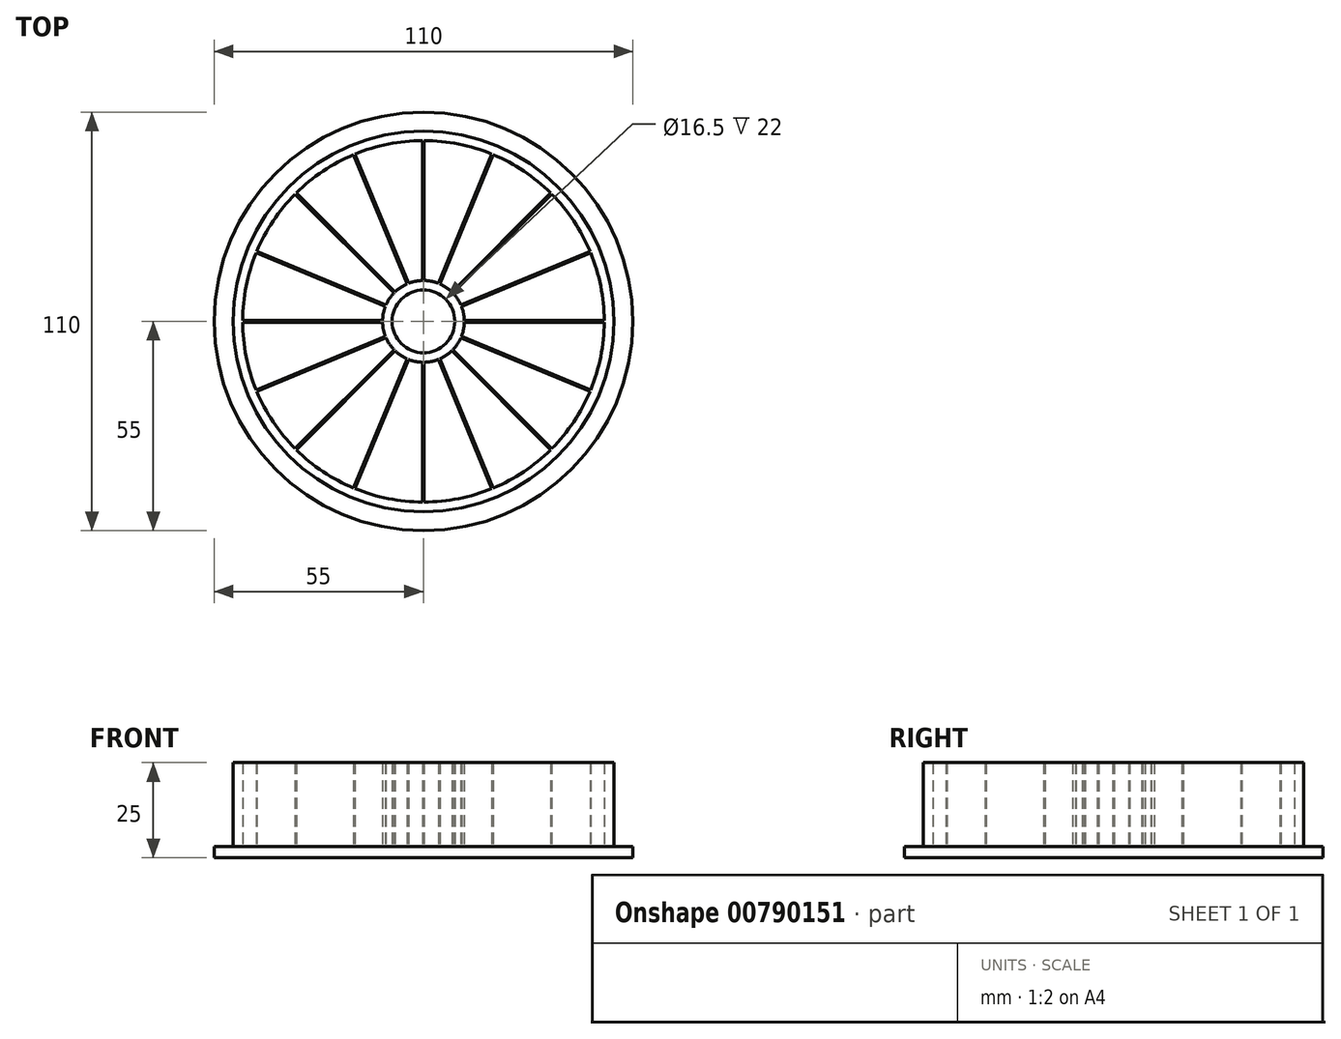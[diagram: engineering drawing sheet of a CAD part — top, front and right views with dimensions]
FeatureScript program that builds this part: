
annotation { "Feature Type Name" : "Feature", "Feature Type Description" : "" }
export const myFeature = defineFeature(function(context is Context, id is Id, definition is map)
    precondition{}
    {
        {
            var Q0;
            Q0=qCreatedBy(makeId("Top.planeOp"),FACE);
            var sketch = newSketch(context, id + "F0", { "sketchPlane" : qUnion([Q0])});
            skCircle(sketch, "E0", {"center": v(0, 0) * mm, "radius": 50 * mm});
            skArc(sketch, "E1", {"start": v(-0.2, 47.5) * mm, "mid": v(-9.27, 46.59) * mm, "end": v(-18, 43.96) * mm});
            skCircle(sketch, "E2", {"center": v(0, 0) * mm, "radius": 8.25 * mm});
            skArc(sketch, "E3", {"start": v(-0.2, 10.75) * mm, "mid": v(-2.1, 10.54) * mm, "end": v(-3.93, 10) * mm});
            skLineSegment(sketch, "E4", {"start": v(-0.2, 10.75) * mm, "end": v(-0.2, 47.5) * mm});
            skLineSegment(sketch, "E5", {"start": v(0.2, 10.75) * mm, "end": v(0.2, 47.5) * mm});
            skLineSegment(sketch, "E6.MirrorCS", {"start": v(-0.2, -10.75) * mm, "end": v(-0.2, -47.5) * mm});
            skLineSegment(sketch, "E7.MirrorCS", {"start": v(0.2, -10.75) * mm, "end": v(0.2, -47.5) * mm});
            skLineSegment(sketch, "E8", {"start": v(-5.83, -5.83) * mm, "end": v(5.83, 5.83) * mm, "construction": true});
            skLineSegment(sketch, "E9", {"start": v(-7.62, -3.16) * mm, "end": v(7.62, 3.16) * mm, "construction": true});
            skLineSegment(sketch, "E10", {"start": v(-8.1, -1.6) * mm, "end": v(8.1, 1.6) * mm, "construction": true});
            skLineSegment(sketch, "E11.MirrorCS", {"start": v(10.75, 0.2) * mm, "end": v(47.5, 0.2) * mm});
            skLineSegment(sketch, "E12.MirrorCS", {"start": v(10.75, -0.2) * mm, "end": v(47.5, -0.2) * mm});
            skLineSegment(sketch, "E13.MirrorCS", {"start": v(-10.75, 0.2) * mm, "end": v(-47.5, 0.2) * mm});
            skLineSegment(sketch, "E14.MirrorCS", {"start": v(-10.75, -0.2) * mm, "end": v(-47.5, -0.2) * mm});
            skLineSegment(sketch, "E15.MirrorCS", {"start": v(7.46, -7.74) * mm, "end": v(33.45, -33.73) * mm});
            skLineSegment(sketch, "E16.MirrorCS", {"start": v(7.74, -7.46) * mm, "end": v(33.73, -33.45) * mm});
            skLineSegment(sketch, "E17.MirrorCS", {"start": v(7.74, 7.46) * mm, "end": v(33.73, 33.45) * mm});
            skLineSegment(sketch, "E18.MirrorCS", {"start": v(7.46, 7.74) * mm, "end": v(33.45, 33.73) * mm});
            skLineSegment(sketch, "E19.MirrorCS", {"start": v(-7.46, 7.74) * mm, "end": v(-33.45, 33.73) * mm});
            skLineSegment(sketch, "E20.MirrorCS", {"start": v(-7.74, 7.46) * mm, "end": v(-33.73, 33.45) * mm});
            skLineSegment(sketch, "E21.MirrorCS", {"start": v(-7.74, -7.46) * mm, "end": v(-33.73, -33.45) * mm});
            skLineSegment(sketch, "E22.MirrorCS", {"start": v(-7.46, -7.74) * mm, "end": v(-33.45, -33.73) * mm});
            skLineSegment(sketch, "E23.MirrorCS", {"start": v(3.93, -10) * mm, "end": v(18, -43.96) * mm});
            skLineSegment(sketch, "E24.MirrorCS", {"start": v(4.3, -9.85) * mm, "end": v(18.36, -43.8) * mm});
            skLineSegment(sketch, "E25.MirrorCS", {"start": v(9.85, -4.3) * mm, "end": v(43.8, -18.36) * mm});
            skLineSegment(sketch, "E26.MirrorCS", {"start": v(10, -3.93) * mm, "end": v(43.96, -18) * mm});
            skLineSegment(sketch, "E27.MirrorCS", {"start": v(10, 3.93) * mm, "end": v(43.96, 18) * mm});
            skLineSegment(sketch, "E28.MirrorCS", {"start": v(9.85, 4.3) * mm, "end": v(43.8, 18.36) * mm});
            skLineSegment(sketch, "E29.MirrorCS", {"start": v(4.3, 9.85) * mm, "end": v(18.36, 43.8) * mm});
            skLineSegment(sketch, "E30.MirrorCS", {"start": v(3.93, 10) * mm, "end": v(18, 43.96) * mm});
            skLineSegment(sketch, "E31.MirrorCS", {"start": v(-3.93, 10) * mm, "end": v(-18, 43.96) * mm});
            skLineSegment(sketch, "E32.MirrorCS", {"start": v(-4.3, 9.85) * mm, "end": v(-18.36, 43.8) * mm});
            skLineSegment(sketch, "E33.MirrorCS", {"start": v(-9.85, 4.3) * mm, "end": v(-43.8, 18.36) * mm});
            skLineSegment(sketch, "E34.MirrorCS", {"start": v(-10, 3.93) * mm, "end": v(-43.96, 18) * mm});
            skLineSegment(sketch, "E35.MirrorCS", {"start": v(-10, -3.93) * mm, "end": v(-43.96, -18) * mm});
            skLineSegment(sketch, "E36.MirrorCS", {"start": v(-9.85, -4.3) * mm, "end": v(-43.8, -18.36) * mm});
            skLineSegment(sketch, "E37.MirrorCS", {"start": v(-4.3, -9.85) * mm, "end": v(-18.36, -43.8) * mm});
            skLineSegment(sketch, "E38.MirrorCS", {"start": v(-3.93, -10) * mm, "end": v(-18, -43.96) * mm});
            skArc(sketch, "E39.trimOffspring", {"start": v(18, 43.96) * mm, "mid": v(9.27, 46.59) * mm, "end": v(0.2, 47.5) * mm});
            skArc(sketch, "E40.trimOffspring", {"start": v(33.45, 33.73) * mm, "mid": v(26.39, 39.5) * mm, "end": v(18.36, 43.8) * mm});
            skArc(sketch, "E41.trimOffspring", {"start": v(47.5, 0.2) * mm, "mid": v(46.59, 9.27) * mm, "end": v(43.96, 18) * mm});
            skArc(sketch, "E42.trimOffspring", {"start": v(43.8, 18.36) * mm, "mid": v(39.5, 26.39) * mm, "end": v(33.73, 33.45) * mm});
            skArc(sketch, "E43.trimOffspring", {"start": v(43.96, -18) * mm, "mid": v(46.59, -9.27) * mm, "end": v(47.5, -0.2) * mm});
            skArc(sketch, "E44.trimOffspring", {"start": v(33.73, -33.45) * mm, "mid": v(39.5, -26.39) * mm, "end": v(43.8, -18.36) * mm});
            skArc(sketch, "E45.trimOffspring", {"start": v(18.36, -43.8) * mm, "mid": v(26.39, -39.5) * mm, "end": v(33.45, -33.73) * mm});
            skArc(sketch, "E46.trimOffspring", {"start": v(0.2, -47.5) * mm, "mid": v(9.27, -46.59) * mm, "end": v(18, -43.96) * mm});
            skArc(sketch, "E47.trimOffspring", {"start": v(-18, -43.96) * mm, "mid": v(-9.27, -46.59) * mm, "end": v(-0.2, -47.5) * mm});
            skArc(sketch, "E48.trimOffspring", {"start": v(-33.45, -33.73) * mm, "mid": v(-26.39, -39.5) * mm, "end": v(-18.36, -43.8) * mm});
            skArc(sketch, "E49.trimOffspring", {"start": v(-43.8, -18.36) * mm, "mid": v(-39.5, -26.39) * mm, "end": v(-33.73, -33.45) * mm});
            skArc(sketch, "E50.trimOffspring", {"start": v(-47.5, -0.2) * mm, "mid": v(-46.59, -9.27) * mm, "end": v(-43.96, -18) * mm});
            skArc(sketch, "E51.trimOffspring", {"start": v(-43.96, 18) * mm, "mid": v(-46.59, 9.27) * mm, "end": v(-47.5, 0.2) * mm});
            skArc(sketch, "E52.trimOffspring", {"start": v(-18.36, 43.8) * mm, "mid": v(-26.39, 39.5) * mm, "end": v(-33.45, 33.73) * mm});
            skArc(sketch, "E53.trimOffspring", {"start": v(-33.73, 33.45) * mm, "mid": v(-39.5, 26.39) * mm, "end": v(-43.8, 18.36) * mm});
            skArc(sketch, "E54.trimOffspring", {"start": v(3.93, 10) * mm, "mid": v(2.1, 10.54) * mm, "end": v(0.2, 10.75) * mm});
            skArc(sketch, "E55.trimOffspring", {"start": v(7.46, 7.74) * mm, "mid": v(5.97, 8.94) * mm, "end": v(4.3, 9.85) * mm});
            skArc(sketch, "E56.trimOffspring", {"start": v(9.85, 4.3) * mm, "mid": v(8.94, 5.97) * mm, "end": v(7.74, 7.46) * mm});
            skArc(sketch, "E57.trimOffspring", {"start": v(10.75, 0.2) * mm, "mid": v(10.54, 2.1) * mm, "end": v(10, 3.93) * mm});
            skArc(sketch, "E58.trimOffspring", {"start": v(10, -3.93) * mm, "mid": v(10.54, -2.1) * mm, "end": v(10.75, -0.2) * mm});
            skArc(sketch, "E59.trimOffspring", {"start": v(7.74, -7.46) * mm, "mid": v(8.94, -5.97) * mm, "end": v(9.85, -4.3) * mm});
            skArc(sketch, "E60.trimOffspring", {"start": v(4.3, -9.85) * mm, "mid": v(5.97, -8.94) * mm, "end": v(7.46, -7.74) * mm});
            skArc(sketch, "E61.trimOffspring", {"start": v(0.2, -10.75) * mm, "mid": v(2.1, -10.54) * mm, "end": v(3.93, -10) * mm});
            skArc(sketch, "E62.trimOffspring", {"start": v(-3.93, -10) * mm, "mid": v(-2.1, -10.54) * mm, "end": v(-0.2, -10.75) * mm});
            skArc(sketch, "E63.trimOffspring", {"start": v(-7.46, -7.74) * mm, "mid": v(-5.97, -8.94) * mm, "end": v(-4.3, -9.85) * mm});
            skArc(sketch, "E64.trimOffspring", {"start": v(-9.85, -4.3) * mm, "mid": v(-8.94, -5.97) * mm, "end": v(-7.74, -7.46) * mm});
            skArc(sketch, "E65.trimOffspring", {"start": v(-10.75, -0.2) * mm, "mid": v(-10.54, -2.1) * mm, "end": v(-10, -3.93) * mm});
            skArc(sketch, "E66.trimOffspring", {"start": v(-10, 3.93) * mm, "mid": v(-10.54, 2.1) * mm, "end": v(-10.75, 0.2) * mm});
            skArc(sketch, "E67.trimOffspring", {"start": v(-7.74, 7.46) * mm, "mid": v(-8.94, 5.97) * mm, "end": v(-9.85, 4.3) * mm});
            skArc(sketch, "E68.trimOffspring", {"start": v(-4.3, 9.85) * mm, "mid": v(-5.97, 8.94) * mm, "end": v(-7.46, 7.74) * mm});
            skSolve(sketch);
        }
        {
            var Q0;
            Q0=makeQuery(id+"F0.imprint","IMPRINT",FACE,{"disambiguationData":[TD([[makeQuery(id+"F0.imprint","IMPRINT",EDGE,{"derivedFrom":sQuery(id+"F0.wireOp",EDGE,"E0")}),1.0]])]});
            extrude(context, id + "F1", {"entities" : qUnion([Q0]), "depth" : 22 * mm, "offsetDistance" : 25 * mm});
        }
        {
            var Q0;
            Q0=qCreatedBy(makeId("Top.planeOp"),FACE);
            var sketch = newSketch(context, id + "F2", { "sketchPlane" : qUnion([Q0])});
            skCircle(sketch, "E69", {"center": v(0, 0) * mm, "radius": 55 * mm});
            skSolve(sketch);
        }
        {
            var Q0;
            Q0=makeQuery(id+"F2.imprint","IMPRINT",FACE,{"disambiguationData":[TD([[makeQuery(id+"F2.imprint","IMPRINT",EDGE,{"derivedFrom":sQuery(id+"F2.wireOp",EDGE,"E69")}),1.0]])]});
            extrude(context, id + "F3", {"entities" : qUnion([Q0]), "operationType" : NewBodyOperationType.ADD, "depth" : -3 * mm, "offsetDistance" : 25 * mm});
        }
    });
